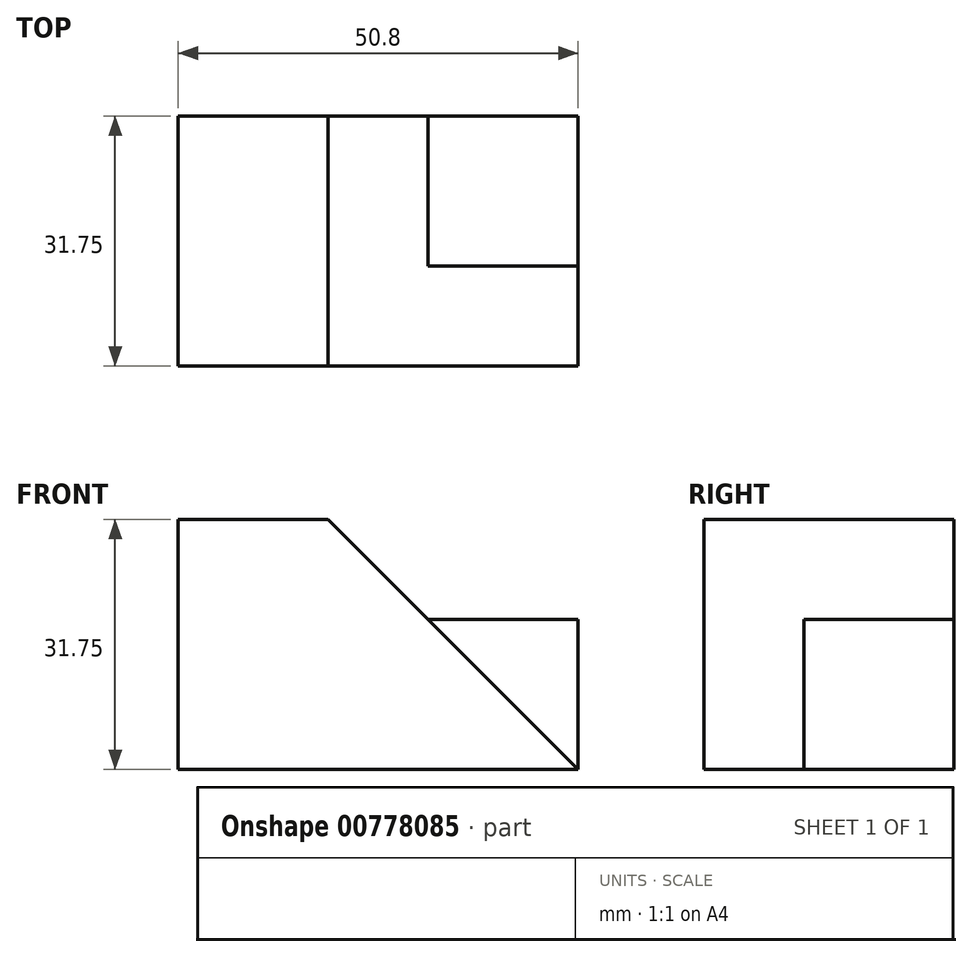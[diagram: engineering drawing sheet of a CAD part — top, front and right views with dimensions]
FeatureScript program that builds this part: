
annotation { "Feature Type Name" : "Feature", "Feature Type Description" : "" }
export const myFeature = defineFeature(function(context is Context, id is Id, definition is map)
    precondition{}
    {
        {
            var Q0;
            Q0=qCreatedBy(makeId("Front.planeOp"),FACE);
            var sketch = newSketch(context, id + "F0", { "sketchPlane" : qUnion([Q0])});
            skLineSegment(sketch, "E0", {"start": v(0, 0) * mm, "end": v(50.8, 0) * mm});
            skLineSegment(sketch, "E1", {"start": v(50.8, 0) * mm, "end": v(50.8, 31.75) * mm});
            skLineSegment(sketch, "E2", {"start": v(50.8, 31.75) * mm, "end": v(0, 31.75) * mm});
            skLineSegment(sketch, "E3", {"start": v(0, 31.75) * mm, "end": v(0, 0) * mm});
            skSolve(sketch);
        }
        {
            var Q0;
            Q0=makeQuery(id+"F0.imprint","IMPRINT",FACE,{"disambiguationData":[TD([[makeQuery(id+"F0.imprint","IMPRINT",EDGE,{"derivedFrom":sQuery(id+"F0.wireOp",EDGE,"E0")}),1.0]])]});
            extrude(context, id + "F1", {"entities" : qUnion([Q0]), "depth" : 31.75 * mm, "offsetDistance" : 25.4 * mm});
        }
        {
            var Q0;
            Q0=makeQuery(id+"F1.opExtrude","CAP_FACE",FACE,{"disambiguationData":[OSD([sQuery(id+"F0.wireOp",EDGE,"E0"),sQuery(id+"F0.wireOp",EDGE,"E1"),sQuery(id+"F0.wireOp",EDGE,"E2"),sQuery(id+"F0.wireOp",EDGE,"E3")])],"isStart":false});
            var sketch = newSketch(context, id + "F2", { "sketchPlane" : qUnion([Q0])});
            skLineSegment(sketch, "E4", {"start": v(0, 31.75) * mm, "end": v(19.05, 31.75) * mm});
            skLineSegment(sketch, "E5", {"start": v(19.05, 31.75) * mm, "end": v(50.8, 0) * mm});
            skSolve(sketch);
        }
        {
            var Q0;
            {var subQ0=sQuery(id+"F2.wireOp",EDGE,"E5");Q0=makeQuery(id+"F2.imprint","IMPRINT",FACE,{"disambiguationData":[TD([[makeQuery(id+"F2.imprint","IMPRINT",EDGE,{"derivedFrom":subQ0}),1.0]])]});}
            extrude(context, id + "F3", {"entities" : qUnion([Q0]), "operationType" : NewBodyOperationType.REMOVE, "oppositeDirection" : true, "depth" : 31.75 * mm, "offsetDistance" : 25.4 * mm});
        }
        {
            var Q0;
            Q0=makeQuery(id+"F1.opExtrude","CAP_FACE",FACE,{"disambiguationData":[OSD([sQuery(id+"F0.wireOp",EDGE,"E0"),sQuery(id+"F0.wireOp",EDGE,"E1"),sQuery(id+"F0.wireOp",EDGE,"E2"),sQuery(id+"F0.wireOp",EDGE,"E3")])],"isStart":false});
            var sketch = newSketch(context, id + "F4", { "sketchPlane" : qUnion([Q0])});
            skLineSegment(sketch, "E6", {"start": v(50.8, 0) * mm, "end": v(50.8, 19.05) * mm});
            skLineSegment(sketch, "E7", {"start": v(50.8, 19.05) * mm, "end": v(31.75, 19.05) * mm});
            skSolve(sketch);
        }
        {
            var Q0;
            {var subQ0=sQuery(id+"F4.wireOp",EDGE,"E6");Q0=makeQuery(id+"F4.imprint","IMPRINT",FACE,{"disambiguationData":[TD([[makeQuery(id+"F4.imprint","IMPRINT",EDGE,{"derivedFrom":subQ0}),1.0]])]});}
            extrude(context, id + "F5", {"entities" : qUnion([Q0]), "operationType" : NewBodyOperationType.ADD, "oppositeDirection" : true, "depth" : 31.75 * mm, "offsetDistance" : 25.4 * mm});
        }
        {
            var Q0;
            Q0=makeQuery(id+"F5.boolean.opBoolean","MERGE",FACE,{"derivedFrom":[makeQuery(id+"F1.opExtrude","CAP_FACE",FACE,{"disambiguationData":[OSD([sQuery(id+"F0.wireOp",EDGE,"E0"),sQuery(id+"F0.wireOp",EDGE,"E1"),sQuery(id+"F0.wireOp",EDGE,"E2"),sQuery(id+"F0.wireOp",EDGE,"E3")])],"isStart":false}),makeQuery(id+"F5.opExtrude","CAP_FACE",FACE,{"disambiguationData":[OSD([sQuery(id+"F2.wireOp",EDGE,"E5"),sQuery(id+"F4.wireOp",EDGE,"E6"),sQuery(id+"F4.wireOp",EDGE,"E7")])],"isStart":true})]});
            var sketch = newSketch(context, id + "F6", { "sketchPlane" : qUnion([Q0])});
            skLineSegment(sketch, "E8", {"start": v(50.8, 0) * mm, "end": v(31.75, 19.05) * mm});
            skSolve(sketch);
        }
        {
            var Q0;
            Q0=makeQuery(id+"F6.imprint","IMPRINT",FACE,{"disambiguationData":[TD([[makeQuery(id+"F6.imprint","IMPRINT",EDGE,{"derivedFrom":sQuery(id+"F6.wireOp",EDGE,"E8")}),-1.0]])]});
            extrude(context, id + "F7", {"entities" : qUnion([Q0]), "operationType" : NewBodyOperationType.REMOVE, "oppositeDirection" : true, "depth" : 12.7 * mm, "offsetDistance" : 25.4 * mm});
        }
    });
